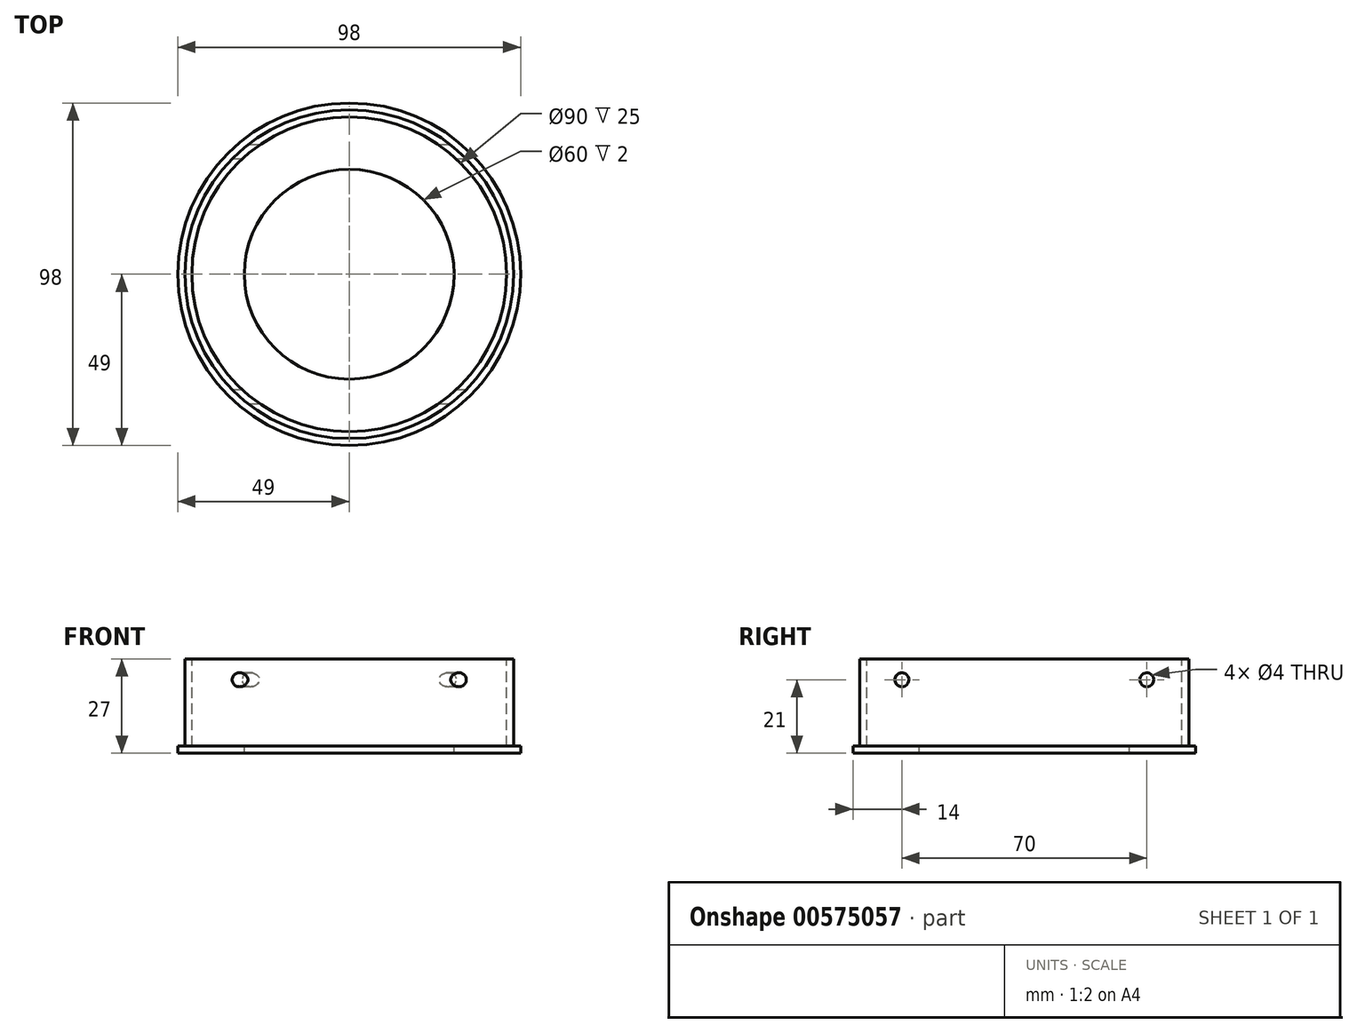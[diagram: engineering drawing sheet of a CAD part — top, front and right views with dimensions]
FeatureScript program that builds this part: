
annotation { "Feature Type Name" : "Feature", "Feature Type Description" : "" }
export const myFeature = defineFeature(function(context is Context, id is Id, definition is map)
    precondition{}
    {
        {
            var Q0;
            Q0=qCreatedBy(makeId("Front.planeOp"),FACE);
            var sketch = newSketch(context, id + "F0", { "sketchPlane" : qUnion([Q0])});
            skLineSegment(sketch, "E0", {"start": v(-30, 2) * mm, "end": v(-30, 0) * mm});
            skLineSegment(sketch, "E1", {"start": v(-30, 0) * mm, "end": v(-49, 0) * mm});
            skLineSegment(sketch, "E2", {"start": v(-47, 27) * mm, "end": v(-45, 27) * mm});
            skLineSegment(sketch, "E3", {"start": v(-45, 27) * mm, "end": v(-45, 2) * mm});
            skLineSegment(sketch, "E4", {"start": v(-45, 2) * mm, "end": v(-30, 2) * mm});
            skLineSegment(sketch, "E5", {"start": v(-47, 27) * mm, "end": v(-47, 2) * mm});
            skLineSegment(sketch, "E6", {"start": v(-47, 2) * mm, "end": v(-49, 2) * mm});
            skLineSegment(sketch, "E7", {"start": v(-49, 2) * mm, "end": v(-49, 0) * mm});
            skLineSegment(sketch, "E8", {"start": v(0, 38.52) * mm, "end": v(0, 0) * mm, "construction": true});
            skSolve(sketch);
        }
        {
            var Q0;
            Q0 = qSketchRegion(id + "F0", true);
            var Q1;
            Q1=sQuery(id+"F0.wireOp",EDGE,"E8");
            revolve(context, id + "F1", {"surfaceOperationType" : NewSurfaceOperationType.NEW, "entities" : qUnion([Q0]), "axis" : qUnion([Q1]), "revolveType" : RevolveType.FULL});
        }
        {
            var Q0;
            Q0=qCreatedBy(makeId("Right.planeOp"),FACE);
            var sketch = newSketch(context, id + "F2", { "sketchPlane" : qUnion([Q0])});
            skCircle(sketch, "E9", {"center": v(-35, 21) * mm, "radius": 2 * mm});
            skLineSegment(sketch, "E10.0", {"start": v(-45, 27) * mm, "end": v(45, 27) * mm, "construction": true});
            skSolve(sketch);
        }
        {
            var Q0;
            Q0=makeQuery(id+"F2.imprint","IMPRINT",FACE,{"disambiguationData":[TD([[makeQuery(id+"F2.imprint","IMPRINT",EDGE,{"derivedFrom":sQuery(id+"F2.wireOp",EDGE,"E9")}),1.0]])]});
            extrude(context, id + "F3", {"entities" : qUnion([Q0]), "endBound" : BoundingType.THROUGH_ALL, "oppositeDirection" : true, "depth" : 25 * mm, "offsetDistance" : 25 * mm, "hasSecondDirection" : true, "secondDirectionBound" : SecondDirectionBoundingType.THROUGH_ALL, "secondDirectionOppositeDirection" : false, "secondDirectionDepth" : 25 * mm});
        }
        {
            var Q0;
            Q0=makeQuery(id+"F3.opExtrude","SWEPT_BODY",BODY,{"disambiguationData":[OSD([sQuery(id+"F2.wireOp",EDGE,"E9")])]});
            var Q1;
            Q1=sQuery(id+"F0.wireOp",EDGE,"E8");
            circularPattern(context, id + "F4", {"operationType" : NewBodyOperationType.REMOVE, "entities" : qUnion([Q0]), "axis" : qUnion([Q1]), "angle" : 360 * degree, "instanceCount" : 2, "equalSpace" : true});
        }
    });
